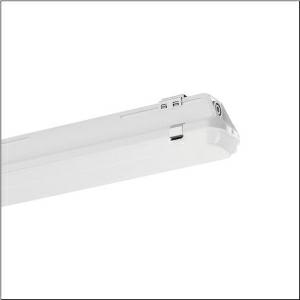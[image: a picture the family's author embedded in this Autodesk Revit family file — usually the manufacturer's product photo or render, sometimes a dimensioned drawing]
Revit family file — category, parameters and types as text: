
# Revit family: monsun_r__12_51fp208p460h_5977
name_source: partatom
category: Lighting Fixtures
units: mm (PartAtom-declared; Revit-internal decimal feet)

## family parameters
Cut with Voids When Loaded = No
Host = Face
Light Source = No
Part Type = Normal
Room Calculation Point = No
Round Connector Dimension = Use Diameter
Shared = No

## types (1)
- Monsun® 12 (1 x LED, 5490 lm, 33.9 W, 4000K)
    Apparent Load = 34 VA
    CIE Flux Codes = 45 75 93 94 100
    Color Rendering = 80
    Color Temperature = 4000K
    Default Elevation = 1800 mm
    Description = Monsun® 12, damp-proof luminaire, chain hanger, primary optical cover: enclosure, of PC, light emission: direct distribution, primary light characteristic: symmetric, installation type: suspended mounting, surface-mounted, horizontal mounting, vertical mounting, LED rated luminous flux: 5.490 lm, light colour: 840, colour temperature: 4000K, control gear: ECG, with terminal, 3-pole, max. 2.5mm², mains connection: 220..240V, AC, 50/60Hz, rated input power: 34W, luminaire housing, of glass-fibre reinforced polyester, uncoated, bright grey, length: 1.590 mm, width: 90 mm, height: 88mm, clip for enclosure, of stainless steel (V2A), ceiling mounting element, of stainless steel (V2A), chain hanger, of stainless steel (V2A), protection rating (complete): IP66, insulation class (complete): insulation class I (protective earthing), certification: CE, ENEC, VDE, protection symbol: D, impact resistance: IK08, permissible ambient temperature for indoor applications: -35..+40°C, standard: EN 50419, EN 60598-2-1, no direct snow, no direct sun, no direct rain, for indoor or canopied outdoor use, corresponds to IFS (International Featured Standards) requirements for safety and quality in the food industry, packaging unit: 1 piece
    Height = 89 mm
    Lamp = 1 x LED
    Lamp Light Flux = 5490 lm
    Lamp Power = 33.9 W
    Lamp count = 1
    Length = 1590 mm
    Luminous efficacy = 162 lm/W
    Manufacturer = Siteco
    ModVariant = No
    Model = 51FP208P460H
    Mounting Place = Ceiling
    Mounting Type = Pendant
    Number of Poles = 1
    OnlyDefault = Yes
    Power Factor = 1
    Product Name = Monsun® 12
    Product group = damp-proof luminaire | ceiling pendant
    ProductGroupID = 908
    Protection Class = Protection class I
    Protection Degree = IP 66
    RLX_Detail_Level = 1
    RlxData = <blob elided: 88201 chars, md5=930bcd75>
    Socket = socket
    Standby Power = 0 W
    System Light Flux = 5490 lm
    System Power = 34 W
    Type Comments = Product without accessories
    Type Image = l_1004748.jpg
    URL = http://relux.com
    VarID = ---
    Voltage = 0 V
    Weight = 0.00 kg
    Width = 90 mm

## geometry (parser evidence)
native form markers: Blend x4, Sweep x12
no freeform markers — native parametric forms only
